# Revit family: F1140C
name_source: partatom
category: Plumbing Fixtures
units: mm (PartAtom-declared; Revit-internal decimal feet)

## family parameters
Classification Number = 23.45.55.21
Cut with Voids When Loaded = No
Enable Cutting in Views = No
Host = Face
Maintain Annotation Orientation = No
Part Type = Normal
Room Calculation Point = No
Round Connector Dimension = Use Radius
Shared = No

## types (6) — shared parameters
Body Height = 13.5 "
Body Radius = 2 "
Description = FLOOR DRAIN WITH 7" OR 9" ROUND TRACTOR GRATE, INTEGRAL DEEP SEAL TRAP & CLEANOUT
Floor Drain Material = Paint - Sherwin Williams Paint - #952C2A - Bellwood Red
Manufacturer = MIFAB
Model = F1140-C
URL = WWW.MIFAB.COM
zero-valued in all types: Default Elevation, WFU

## per-type parameters (varying)
| type | Pipe Diameter | Pipe Radius | Strainer Diameter | Strainer Radius |
| 7" Strainer - 2" Drain | 2 " | 1 " | 7 " | 3.5 " |
| 9" Strainer - 3" Drain | 3 " | 1.5 " | 9 " | 4.5 " |
| 9" Strainer - 4" Drain | 4 " | 2 " | 9 " | 4.5 " |
| 9" Strainer - 2" Drain | 2 " | 1 " | 9 " | 4.5 " |
| 7" Strainer - 3" Drain | 3 " | 1.5 " | 7 " | 3.5 " |
| 7" Strainer - 4" Drain | 4 " | 2 " | 7 " | 3.5 " |

## geometry (parser evidence)
native form markers: Blend x3, Sweep x2
no freeform markers — native parametric forms only
